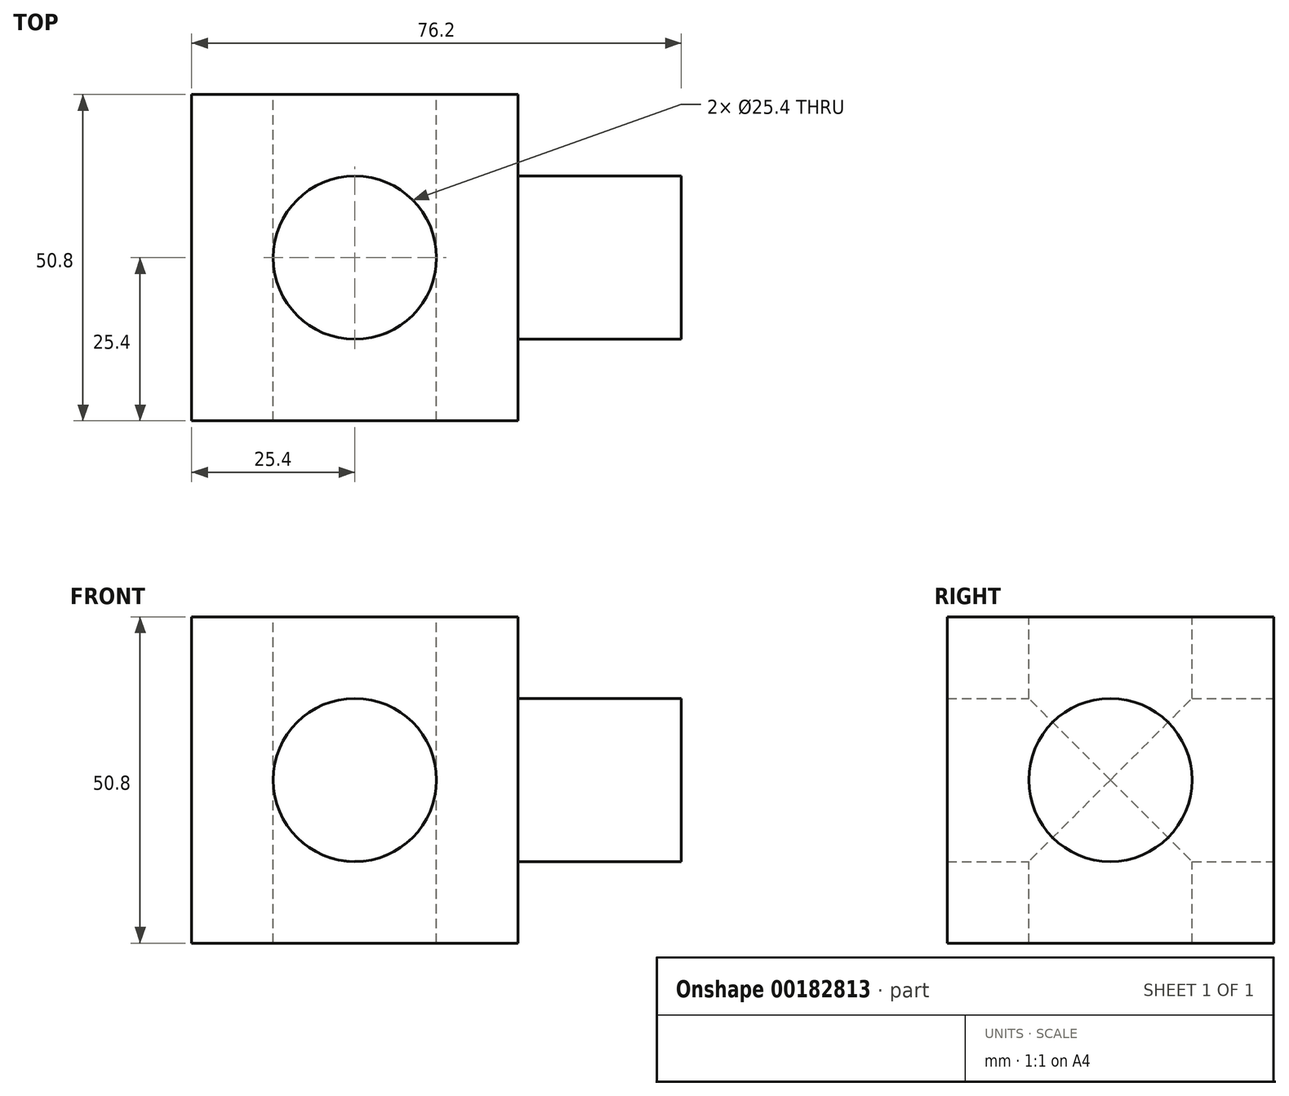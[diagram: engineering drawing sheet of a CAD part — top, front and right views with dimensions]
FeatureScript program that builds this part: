
annotation { "Feature Type Name" : "Feature", "Feature Type Description" : "" }
export const myFeature = defineFeature(function(context is Context, id is Id, definition is map)
    precondition{}
    {
        {
            var Q0;
            Q0=qCreatedBy(makeId("Front.planeOp"),FACE);
            var sketch = newSketch(context, id + "F0", { "sketchPlane" : qUnion([Q0])});
            skLineSegment(sketch, "E0.bottom", {"start": v(25.4, 25.4) * mm, "end": v(-25.4, 25.4) * mm});
            skLineSegment(sketch, "E0.top", {"start": v(25.4, -25.4) * mm, "end": v(-25.4, -25.4) * mm});
            skLineSegment(sketch, "E0.left", {"start": v(25.4, 25.4) * mm, "end": v(25.4, -25.4) * mm});
            skLineSegment(sketch, "E0.right", {"start": v(-25.4, 25.4) * mm, "end": v(-25.4, -25.4) * mm});
            skPoint(sketch, "E0.middle", {"position": v(0, 0) * mm});
            skCircle(sketch, "E1", {"center": v(0, 0) * mm, "radius": 12.7 * mm});
            skSolve(sketch);
        }
        {
            var Q0;
            Q0=makeQuery(id+"F0.imprint","IMPRINT",FACE,{"disambiguationData":[TD([[makeQuery(id+"F0.imprint","IMPRINT",EDGE,{"derivedFrom":sQuery(id+"F0.wireOp",EDGE,"E0.bottom")}),1.0]])]});
            extrude(context, id + "F1", {"entities" : qUnion([Q0]), "endBound" : BoundingType.SYMMETRIC, "depth" : 50.8 * mm});
        }
        {
            var Q0;
            Q0=makeQuery(id+"F1.opExtrude","SWEPT_FACE",FACE,{"disambiguationData":[OSD([sQuery(id+"F0.wireOp",EDGE,"E0.bottom")])]});
            var sketch = newSketch(context, id + "F2", { "sketchPlane" : qUnion([Q0])});
            skCircle(sketch, "E2", {"center": v(0, 0) * mm, "radius": 12.7 * mm});
            skSolve(sketch);
        }
        {
            var Q0;
            Q0=makeQuery(id+"F2.imprint","IMPRINT",FACE,{"disambiguationData":[TD([[makeQuery(id+"F2.imprint","IMPRINT",EDGE,{"derivedFrom":sQuery(id+"F2.wireOp",EDGE,"E2")}),1.0]])]});
            extrude(context, id + "F3", {"entities" : qUnion([Q0]), "operationType" : NewBodyOperationType.REMOVE, "endBound" : BoundingType.THROUGH_ALL, "oppositeDirection" : true, "depth" : 25.4 * mm});
        }
        {
            var Q0;
            Q0=makeQuery(id+"F1.opExtrude","SWEPT_FACE",FACE,{"disambiguationData":[OSD([sQuery(id+"F0.wireOp",EDGE,"E0.left")])]});
            var sketch = newSketch(context, id + "F4", { "sketchPlane" : qUnion([Q0])});
            skCircle(sketch, "E3", {"center": v(0, 0) * mm, "radius": 12.7 * mm});
            skSolve(sketch);
        }
        {
            var Q0;
            Q0=makeQuery(id+"F4.imprint","IMPRINT",FACE,{"disambiguationData":[TD([[makeQuery(id+"F4.imprint","IMPRINT",EDGE,{"derivedFrom":sQuery(id+"F4.wireOp",EDGE,"E3")}),1.0]])]});
            extrude(context, id + "F5", {"entities" : qUnion([Q0]), "operationType" : NewBodyOperationType.ADD, "depth" : 25.4 * mm});
        }
    });
